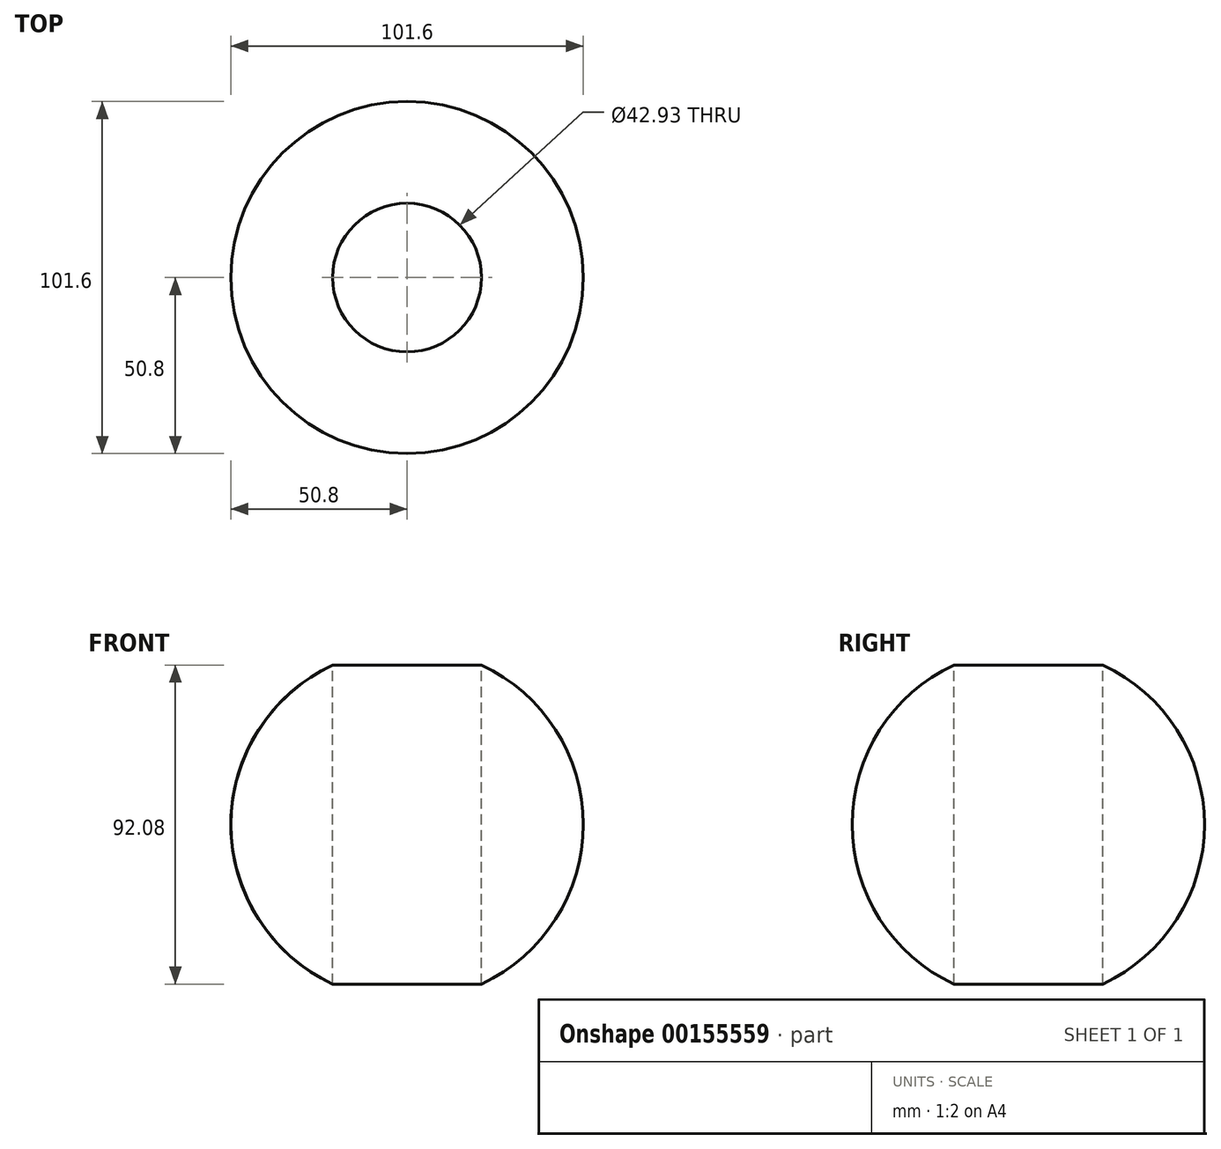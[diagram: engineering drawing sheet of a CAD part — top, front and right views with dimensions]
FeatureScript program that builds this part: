
annotation { "Feature Type Name" : "Feature", "Feature Type Description" : "" }
export const myFeature = defineFeature(function(context is Context, id is Id, definition is map)
    precondition{}
    {
        {
            var Q0;
            Q0=qCreatedBy(makeId("Front.planeOp"),FACE);
            var sketch = newSketch(context, id + "F0", { "sketchPlane" : qUnion([Q0])});
            skCircle(sketch, "E0", {"center": v(0, 0) * mm, "radius": 50.8 * mm});
            skLineSegment(sketch, "E1", {"start": v(0, 0) * mm, "end": v(0, 50.8) * mm, "construction": true});
            skLineSegment(sketch, "E2", {"start": v(0, 50.8) * mm, "end": v(0, -50.8) * mm});
            skSolve(sketch);
        }
        {
            var Q0;
            {var subQ0=sQuery(id+"F0.wireOp",EDGE,"E2");Q0=makeQuery(id+"F0.imprint","IMPRINT",FACE,{"disambiguationData":[TD([[makeQuery(id+"F0.imprint","IMPRINT",EDGE,{"derivedFrom":subQ0}),1.0]])]});}
            var Q1;
            Q1=sQuery(id+"F0.wireOp",EDGE,"E2");
            revolve(context, id + "F1", {"entities" : qUnion([Q0]), "axis" : qUnion([Q1]), "revolveType" : RevolveType.FULL});
        }
        {
            var Q0;
            Q0=qCreatedBy(makeId("Top.planeOp"),FACE);
            cPlane(context, id + "F2", {"entities" : qUnion([Q0]), "cplaneType" : CPlaneType.OFFSET, "offset" : 63.5 * mm, "width" : 152.4 * mm, "height" : 152.4 * mm});
        }
        {
            var Q0;
            Q0=qCreatedBy(id+"F2.planeOp",FACE);
            var sketch = newSketch(context, id + "F3", { "sketchPlane" : qUnion([Q0])});
            skCircle(sketch, "E3", {"center": v(0, 0) * mm, "radius": 21.46 * mm});
            skSolve(sketch);
        }
        {
            var Q0;
            Q0=makeQuery(id+"F3.imprint","IMPRINT",FACE,{"disambiguationData":[TD([[makeQuery(id+"F3.imprint","IMPRINT",EDGE,{"derivedFrom":sQuery(id+"F3.wireOp",EDGE,"E3")}),1.0]])]});
            extrude(context, id + "F4", {"entities" : qUnion([Q0]), "operationType" : NewBodyOperationType.REMOVE, "oppositeDirection" : true, "depth" : 122.55 * mm});
        }
    });
